# Revit family: Sanitary_Bath-Spas_Ponte-Giulio_Walk-in-bathtub-inward-door
name_source: partatom
category: Plumbing Fixtures
units: mm (PartAtom-declared; Revit-internal decimal feet)

## family parameters
Always vertical = No
Cut with Voids When Loaded = No
OmniClass Number = 23.45.00.00
OmniClass Title = Sanitary, Laundry, and Cleaning Equipment
Part Type = Normal
Room Calculation Point = No
Round Connector Dimension = Use Diameter
Shared = No
Work Plane-Based = No

## types (1)
- Walk-in bathtub inward door
    BIMobject category = Bath & Spas
    BIMobject category code = sanitary-bath-spas
    BIMobject main category = Sanitary
    BIMobject main category code = sanitary
    BOSUseNativeGeometries = 1
    Brand url = http://www.pontegiulio.com
    Default Elevation = 0 mm  [stored 0 ft]
    Design country = Italy
    Diameter = 50 mm  [stored 0.164042 ft]
    Edition number = 1
    IFC Classification = Sanitary Terminal
    Manufacturer country = Italy
    Manufacturer name = Ponte Giulio
    Material main = Fibreglass reinforced polymer composite
    Material secondary = Steel
    NBS Reference Code = 35-06-08
    NBS Reference Description = Baths
    OmniClass Code = 23-31 15 00
    OmniClass Description = Bathtubs
    Product Guid = b66594f7-f48e-4b98-bcc0-afbaf248dba8
    Product SKU = M74MDS18
    Product data url = https://bimobject.com
    Product family = Safe bathroom
    Product group = Basins
    Product name = Walk-in bathtub inward door
    Product url = https://www.pontegiulio.com
    QR code = http://bimobject.com
    Technical description = http://www.pgdb.it
    UNSPSC Code = 30181501
    Uniclass 1.4 Code = L7211
    Uniclass 1.4 Description = Baths
    Uniclass 2.0 Code = PR-35-06-08
    Uniclass 2.0 Description = Baths
    Uniclass 2015 Code = SL_35_80_08
    Uniclass 2015 Name = Bathrooms

note: [stored X ft] marks values corroborated as IEEE doubles in the binary element streams (Revit-internal decimal feet)

## geometry (parser evidence)
native form markers: Sweep x3
no freeform markers — native parametric forms only
